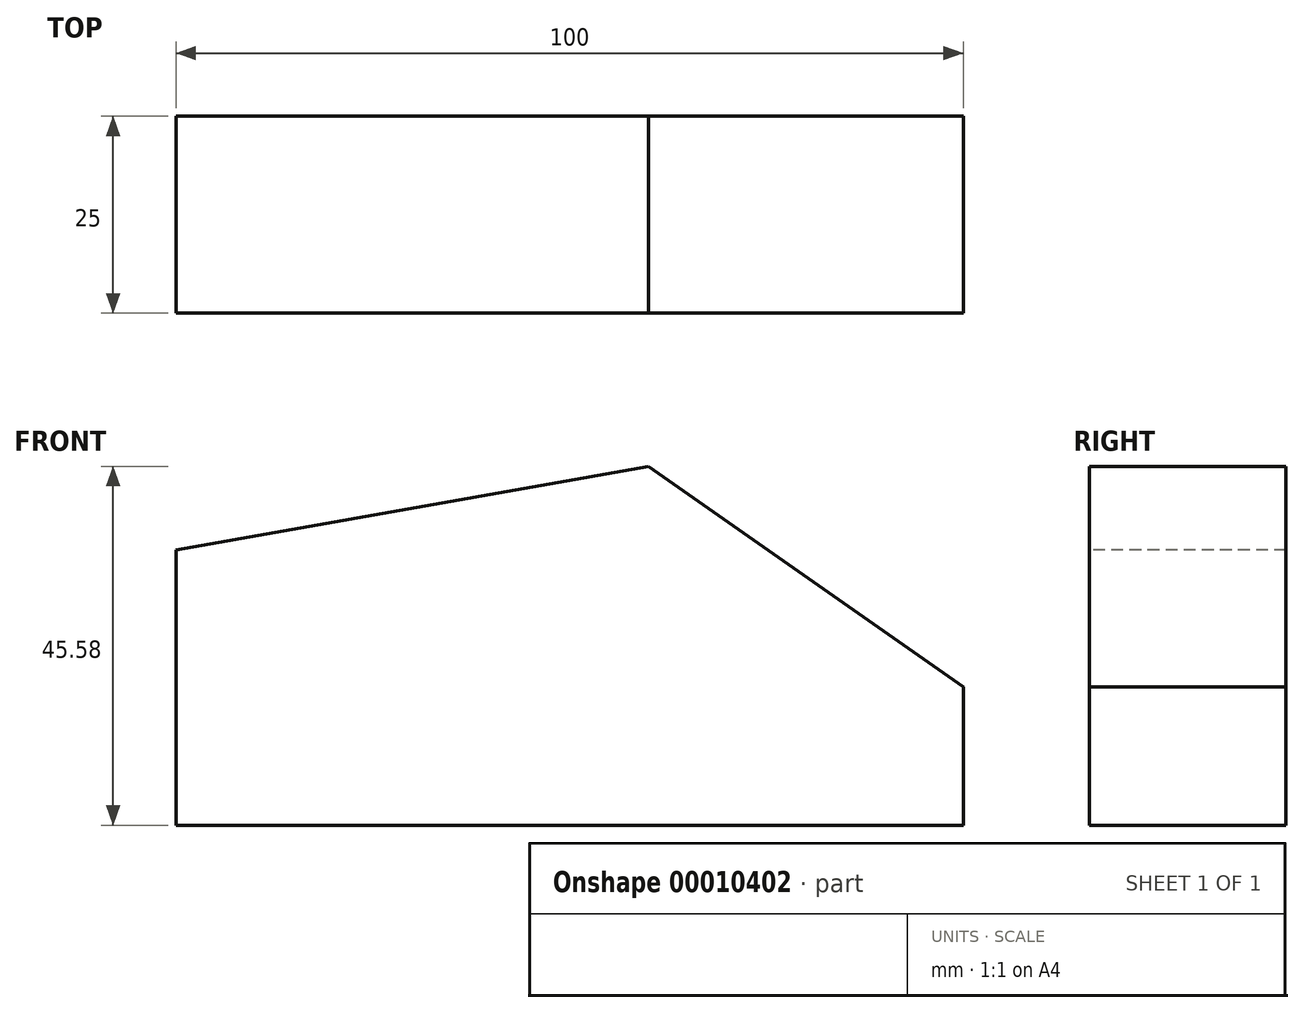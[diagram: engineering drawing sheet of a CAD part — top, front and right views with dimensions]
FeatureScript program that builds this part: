
annotation { "Feature Type Name" : "Feature", "Feature Type Description" : "" }
export const myFeature = defineFeature(function(context is Context, id is Id, definition is map)
    precondition{}
    {
        {
            var Q0;
            Q0=qCreatedBy(makeId("Front.planeOp"),FACE);
            var sketch = newSketch(context, id + "F0", { "sketchPlane" : qUnion([Q0])});
            skLineSegment(sketch, "E0", {"start": v(0, 0) * mm, "end": v(100, 0) * mm});
            skLineSegment(sketch, "E1", {"start": v(100, 0) * mm, "end": v(100, 17.57) * mm});
            skLineSegment(sketch, "E2", {"start": v(100, 17.57) * mm, "end": v(60, 45.58) * mm});
            skLineSegment(sketch, "E3", {"start": v(60, 45.58) * mm, "end": v(0, 35) * mm});
            skLineSegment(sketch, "E4", {"start": v(0, 35) * mm, "end": v(0, 0) * mm});
            skSolve(sketch);
        }
        {
            var Q0;
            Q0 = qSketchRegion(id + "F0", true);
            extrude(context, id + "F1", {"entities" : qUnion([Q0]), "oppositeDirection" : true, "depth" : 25 * mm});
        }
    });
